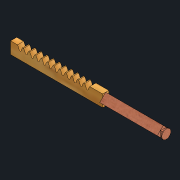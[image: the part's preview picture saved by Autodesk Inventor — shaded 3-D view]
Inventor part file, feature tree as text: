
AUTODESK INVENTOR PART (.ipt)
format: ipt  version: 2022.2 (Build 262287010, 287A)  size: 236,544 bytes
history: native  units: mm
features: sketch x5, extrude x5, pattern_linear x1
ambient origin geometry x8: Origin, YZ Plane, XZ Plane, XY Plane, X Axis, Y Axis, Z Axis, Center Point
bodies: Body1 (feature_tree)
feature tree (11):
  sketch  "Sketch1"  dims[d11=0.0mm d12=8.0mm d13=0.0mm]
  extrude  "Extrusion3"  Depth=8.0mm TaperAngle=0.0deg
  extrude  "Extrusion4"  TaperAngle=0.0deg  [1 undecoded]
  pattern_linear  "Rectangular Pattern1"  [2 undecoded]
  extrude  "Extrusion5"  [1 undecoded]
  extrude  "Extrusion6"  [1 undecoded]
  extrude  "Extrusion7"  [1 undecoded]
  sketch  "Sketch2"  dims[d24=0.0mm d28=0.0mm]
  sketch  "Sketch3"  dims[d31=0.0mm]
  sketch  "Sketch4"
  sketch  "Sketch5"
note: 6 required parameter values undecoded (feature->parameter linkage not recoverable at this tier; creation-order binding heuristic only, values carry confidence <= 0.55)
